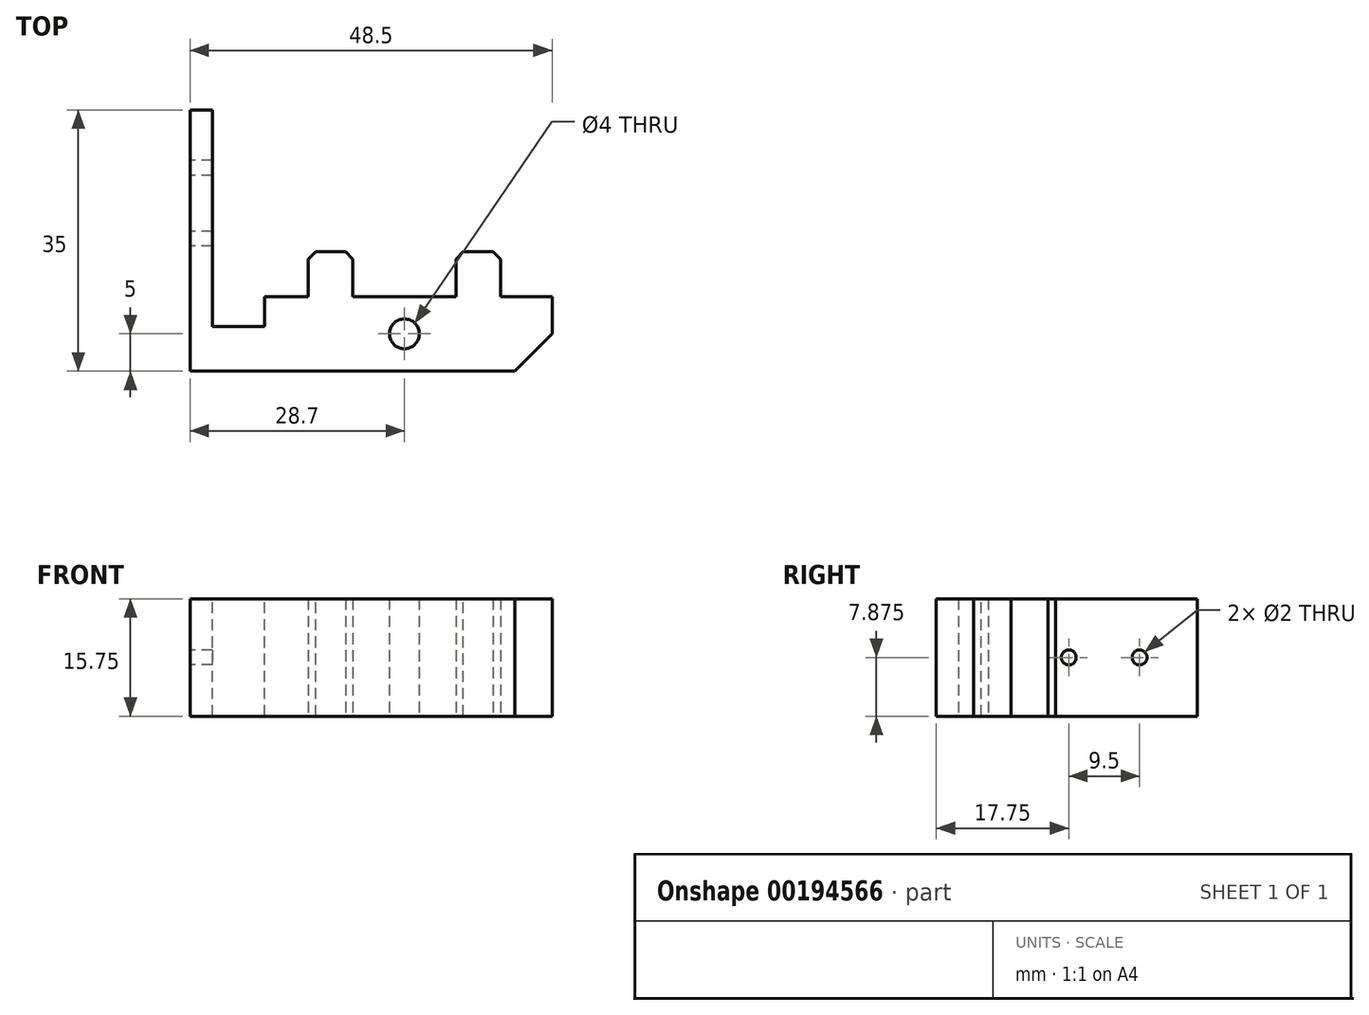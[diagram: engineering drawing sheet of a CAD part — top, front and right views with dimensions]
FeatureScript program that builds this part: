
annotation { "Feature Type Name" : "Feature", "Feature Type Description" : "" }
export const myFeature = defineFeature(function(context is Context, id is Id, definition is map)
    precondition{}
    {
        {
            var Q0;
            Q0=qCreatedBy(makeId("Top.planeOp"),FACE);
            var sketch = newSketch(context, id + "F0", { "sketchPlane" : qUnion([Q0])});
            skLineSegment(sketch, "E0", {"start": v(44.5, 0) * mm, "end": v(44.5, 10) * mm});
            skLineSegment(sketch, "E1", {"start": v(44.5, 10) * mm, "end": v(37.6, 10) * mm});
            skLineSegment(sketch, "E2", {"start": v(37.6, 10) * mm, "end": v(37.6, 16) * mm});
            skLineSegment(sketch, "E3", {"start": v(37.6, 16) * mm, "end": v(31.6, 16) * mm});
            skLineSegment(sketch, "E4", {"start": v(31.6, 16) * mm, "end": v(31.6, 10) * mm});
            skLineSegment(sketch, "E5", {"start": v(31.6, 10) * mm, "end": v(17.8, 10) * mm});
            skLineSegment(sketch, "E6", {"start": v(17.8, 10) * mm, "end": v(17.8, 16) * mm});
            skLineSegment(sketch, "E7", {"start": v(17.8, 16) * mm, "end": v(11.8, 16) * mm});
            skLineSegment(sketch, "E8", {"start": v(11.8, 16) * mm, "end": v(11.8, 10) * mm});
            skLineSegment(sketch, "E9", {"start": v(11.8, 10) * mm, "end": v(0, 10) * mm});
            skLineSegment(sketch, "E10", {"start": v(0, 0) * mm, "end": v(44.5, 0) * mm});
            skLineSegment(sketch, "E11", {"start": v(0, 10) * mm, "end": v(0, 0) * mm});
            skSolve(sketch);
        }
        {
            var Q0;
            Q0=qSketchRegion(id+"F0",true);
            extrude(context, id + "F1", {"entities" : qUnion([Q0]), "depth" : 15.75 * mm});
        }
        {
            var Q0;
            Q0=makeQuery(id+"F1.opExtrude","SWEPT_FACE",FACE,{"disambiguationData":[OSD([sQuery(id+"F0.wireOp",EDGE,"E10")])]});
            var sketch = newSketch(context, id + "F2", { "sketchPlane" : qUnion([Q0])});
            skLineSegment(sketch, "E12", {"start": v(0, 12.75) * mm, "end": v(15, 12.75) * mm});
            skLineSegment(sketch, "E13", {"start": v(15, 12.75) * mm, "end": v(15, 3) * mm});
            skLineSegment(sketch, "E14", {"start": v(15, 3) * mm, "end": v(0, 3) * mm});
            skLineSegment(sketch, "E15", {"start": v(0, 12.75) * mm, "end": v(0, 3) * mm});
            skSolve(sketch);
        }
        {
            var Q0;
            Q0=makeQuery(id+"F1.opExtrude","CAP_FACE",FACE,{"disambiguationData":[OSD([sQuery(id+"F0.wireOp",EDGE,"E0"),sQuery(id+"F0.wireOp",EDGE,"E1"),sQuery(id+"F0.wireOp",EDGE,"E2"),sQuery(id+"F0.wireOp",EDGE,"E3"),sQuery(id+"F0.wireOp",EDGE,"E4"),sQuery(id+"F0.wireOp",EDGE,"E5"),sQuery(id+"F0.wireOp",EDGE,"E6"),sQuery(id+"F0.wireOp",EDGE,"E7"),sQuery(id+"F0.wireOp",EDGE,"E8"),sQuery(id+"F0.wireOp",EDGE,"E9"),sQuery(id+"F0.wireOp",EDGE,"E10"),sQuery(id+"F0.wireOp",EDGE,"E11")])],"isStart":false});
            var sketch = newSketch(context, id + "F3", { "sketchPlane" : qUnion([Q0])});
            skPoint(sketch, "E16", {"position": v(24.7, 5) * mm});
            skPoint(sketch, "E16.positionSnap0", {"position": v(44.5, 5) * mm});
            skPoint(sketch, "E16.positionSnap1", {"position": v(24.7, 10) * mm});
            skSolve(sketch);
        }
        {
            var Q0;
            Q0=sQuery(id+"F3.wireOp",VERTEX,"E16");
            var Q1;
            Q1=makeQuery(id+"F1.opExtrude","SWEPT_BODY",BODY,{"disambiguationData":[OSD([sQuery(id+"F0.wireOp",EDGE,"E0"),sQuery(id+"F0.wireOp",EDGE,"E1"),sQuery(id+"F0.wireOp",EDGE,"E2"),sQuery(id+"F0.wireOp",EDGE,"E3"),sQuery(id+"F0.wireOp",EDGE,"E4"),sQuery(id+"F0.wireOp",EDGE,"E5"),sQuery(id+"F0.wireOp",EDGE,"E6"),sQuery(id+"F0.wireOp",EDGE,"E7"),sQuery(id+"F0.wireOp",EDGE,"E8"),sQuery(id+"F0.wireOp",EDGE,"E9"),sQuery(id+"F0.wireOp",EDGE,"E10"),sQuery(id+"F0.wireOp",EDGE,"E11")])]});
            hole(context, id + "F4", {"style" : HoleStyle.SIMPLE, "endStyle" : HoleEndStyle.THROUGH, "holeDiameter" : 4 * mm, "locations" : qUnion([Q0]), "scope" : qUnion([Q1]), "isTappedThrough" : true, "startStyle" : HoleStartStyle.PART});
        }
        {
            var Q0;
            Q0=makeQuery(id+"F1.opExtrude","SWEPT_FACE",FACE,{"disambiguationData":[OSD([sQuery(id+"F0.wireOp",EDGE,"E11")])]});
            extrude(context, id + "F5", {"entities" : qUnion([Q0]), "operationType" : NewBodyOperationType.ADD, "depth" : 3 * mm});
        }
        {
            var Q0;
            {var subQ0=sQuery(id+"F0.wireOp",EDGE,"E9");Q0=makeQuery(id+"F5.boolean.opBoolean","MERGE",FACE,{"derivedFrom":[makeQuery(id+"F1.opExtrude","SWEPT_FACE",FACE,{"disambiguationData":[OSD([subQ0])]}),makeQuery(id+"F5.opExtrude","SWEPT_FACE",FACE,{"disambiguationData":[OSD([subQ0,sQuery(id+"F0.wireOp",EDGE,"E11")])]})]});}
            var sketch = newSketch(context, id + "F6", { "sketchPlane" : qUnion([Q0])});
            skLineSegment(sketch, "E17", {"start": v(0, 0) * mm, "end": v(0, 15.75) * mm});
            skSolve(sketch);
        }
        {
            var Q0;
            {var subQ0=sQuery(id+"F6.wireOp",EDGE,"E17");Q0=makeQuery(id+"F6.imprint","IMPRINT",FACE,{"disambiguationData":[TD([[makeQuery(id+"F6.imprint","IMPRINT",EDGE,{"derivedFrom":subQ0}),-1.0]])]});}
            extrude(context, id + "F7", {"entities" : qUnion([Q0]), "operationType" : NewBodyOperationType.ADD, "depth" : 25 * mm});
        }
        {
            var Q0;
            Q0=makeQuery(id+"F7.opExtrude","SWEPT_FACE",FACE,{"disambiguationData":[OSD([sQuery(id+"F6.wireOp",EDGE,"E17")])]});
            var sketch = newSketch(context, id + "F8", { "sketchPlane" : qUnion([Q0])});
            skPoint(sketch, "E18", {"position": v(27.25, 7.88) * mm});
            skPoint(sketch, "E18.positionSnap0", {"position": v(35, 7.88) * mm});
            skPoint(sketch, "E19", {"position": v(17.75, 7.88) * mm});
            skLineSegment(sketch, "E20", {"start": v(27.25, 7.88) * mm, "end": v(35, 7.88) * mm, "construction": true});
            skLineSegment(sketch, "E21", {"start": v(17.75, 7.88) * mm, "end": v(10, 7.88) * mm, "construction": true});
            skSolve(sketch);
        }
        {
            var Q0;
            Q0=sQuery(id+"F8.wireOp",VERTEX,"E18");
            var Q1;
            Q1=sQuery(id+"F8.wireOp",VERTEX,"E19");
            var Q2;
            Q2=makeQuery(id+"F1.opExtrude","SWEPT_BODY",BODY,{"disambiguationData":[OSD([sQuery(id+"F0.wireOp",EDGE,"E0"),sQuery(id+"F0.wireOp",EDGE,"E1"),sQuery(id+"F0.wireOp",EDGE,"E2"),sQuery(id+"F0.wireOp",EDGE,"E3"),sQuery(id+"F0.wireOp",EDGE,"E4"),sQuery(id+"F0.wireOp",EDGE,"E5"),sQuery(id+"F0.wireOp",EDGE,"E6"),sQuery(id+"F0.wireOp",EDGE,"E7"),sQuery(id+"F0.wireOp",EDGE,"E8"),sQuery(id+"F0.wireOp",EDGE,"E9"),sQuery(id+"F0.wireOp",EDGE,"E10"),sQuery(id+"F0.wireOp",EDGE,"E11")])]});
            hole(context, id + "F9", {"style" : HoleStyle.SIMPLE, "endStyle" : HoleEndStyle.THROUGH, "holeDiameter" : 2 * mm, "locations" : qUnion([Q0, Q1]), "scope" : qUnion([Q2]), "isTappedThrough" : true, "startStyle" : HoleStartStyle.SKETCH});
        }
        {
            var Q0;
            {var subQ0=sQuery(id+"F0.wireOp",EDGE,"E11");var subQ1=sQuery(id+"F0.wireOp",EDGE,"E9");var subQ2=makeQuery(id+"F5.boolean.opBoolean","MERGE",EDGE,{"derivedFrom":[makeQuery(id+"F1.opExtrude","CAP_EDGE",EDGE,{"disambiguationData":[OSD([subQ1])],"isStart":false}),makeQuery(id+"F5.opExtrude","SWEPT_EDGE",EDGE,{"disambiguationData":[OSD([subQ1,subQ0]),TDD([makeQuery(id+"F1.opExtrude","CAP_VERTEX",VERTEX,{"disambiguationData":[OSD([subQ1,subQ0])],"isStart":false})])]})]});Q0=makeQuery(id+"F7.boolean.opBoolean","MERGE",FACE,{"derivedFrom":[makeQuery(id+"F5.boolean.opBoolean","MERGE",FACE,{"derivedFrom":[makeQuery(id+"F1.opExtrude","CAP_FACE",FACE,{"disambiguationData":[OSD([sQuery(id+"F0.wireOp",EDGE,"E0"),sQuery(id+"F0.wireOp",EDGE,"E1"),sQuery(id+"F0.wireOp",EDGE,"E2"),sQuery(id+"F0.wireOp",EDGE,"E3"),sQuery(id+"F0.wireOp",EDGE,"E4"),sQuery(id+"F0.wireOp",EDGE,"E5"),sQuery(id+"F0.wireOp",EDGE,"E6"),sQuery(id+"F0.wireOp",EDGE,"E7"),sQuery(id+"F0.wireOp",EDGE,"E8"),subQ1,sQuery(id+"F0.wireOp",EDGE,"E10"),subQ0])],"isStart":false}),makeQuery(id+"F5.opExtrude","SWEPT_FACE",FACE,{"disambiguationData":[OSD([subQ0]),TDD([makeQuery(id+"F1.opExtrude","CAP_EDGE",EDGE,{"disambiguationData":[OSD([subQ0])],"isStart":false})])]})]}),makeQuery(id+"F7.opExtrude","SWEPT_FACE",FACE,{"disambiguationData":[OSD([subQ1,subQ0]),TDD([makeQuery(id+"F6.imprint","IMPRINT",EDGE,{"disambiguationData":[TD([[makeQuery(id+"F6.imprint","INTERSECT",VERTEX,{"derivedFrom":[subQ2,sQuery(id+"F6.wireOp",EDGE,"E17")]}),-1.0]])],"derivedFrom":subQ2})])]})]});}
            var sketch = newSketch(context, id + "F10", { "sketchPlane" : qUnion([Q0])});
            skLineSegment(sketch, "E22", {"start": v(0, 10) * mm, "end": v(0, 6) * mm});
            skLineSegment(sketch, "E23", {"start": v(0, 6) * mm, "end": v(6, 6) * mm});
            skLineSegment(sketch, "E24", {"start": v(6, 6) * mm, "end": v(6, 10) * mm});
            skLineSegment(sketch, "E25", {"start": v(6, 10) * mm, "end": v(0, 10) * mm});
            skSolve(sketch);
        }
        {
            var Q0;
            Q0=qSketchRegion(id+"F10",true);
            extrude(context, id + "F11", {"entities" : qUnion([Q0]), "operationType" : NewBodyOperationType.REMOVE, "endBound" : BoundingType.THROUGH_ALL, "oppositeDirection" : true, "depth" : 25 * mm});
        }
        {
            var Q0;
            Q0=makeQuery(id+"F1.opExtrude","SWEPT_EDGE",EDGE,{"disambiguationData":[OSD([sQuery(id+"F0.wireOp",EDGE,"E7"),sQuery(id+"F0.wireOp",EDGE,"E8")])]});
            var Q1;
            Q1=makeQuery(id+"F1.opExtrude","SWEPT_EDGE",EDGE,{"disambiguationData":[OSD([sQuery(id+"F0.wireOp",EDGE,"E6"),sQuery(id+"F0.wireOp",EDGE,"E7")])]});
            var Q2;
            Q2=makeQuery(id+"F1.opExtrude","SWEPT_EDGE",EDGE,{"disambiguationData":[OSD([sQuery(id+"F0.wireOp",EDGE,"E3"),sQuery(id+"F0.wireOp",EDGE,"E4")])]});
            var Q3;
            Q3=makeQuery(id+"F1.opExtrude","SWEPT_EDGE",EDGE,{"disambiguationData":[OSD([sQuery(id+"F0.wireOp",EDGE,"E2"),sQuery(id+"F0.wireOp",EDGE,"E3")])]});
            chamfer(context, id + "F12", {"entities" : qUnion([Q0, Q1, Q2, Q3]), "width" : 1 * mm, "tangentPropagation" : true});
        }
        {
            var Q0;
            Q0=makeQuery(id+"F1.opExtrude","SWEPT_EDGE",EDGE,{"disambiguationData":[OSD([sQuery(id+"F0.wireOp",EDGE,"E0"),sQuery(id+"F0.wireOp",EDGE,"E10")])]});
            chamfer(context, id + "F13", {"entities" : qUnion([Q0]), "width" : 5 * mm, "tangentPropagation" : true});
        }
        {
            var Q0;
            {var subQ0=sQuery(id+"F0.wireOp",EDGE,"E11");var subQ1=sQuery(id+"F0.wireOp",EDGE,"E9");Q0=makeQuery(id+"F7.boolean.opBoolean","MERGE",FACE,{"derivedFrom":[makeQuery(id+"F5.opExtrude","CAP_FACE",FACE,{"disambiguationData":[OSD([subQ0])],"isStart":false}),makeQuery(id+"F7.opExtrude","SWEPT_FACE",FACE,{"disambiguationData":[OSD([subQ1,subQ0]),TDD([makeQuery(id+"F6.imprint","IMPRINT",EDGE,{"derivedFrom":makeQuery(id+"F5.opExtrude","CAP_EDGE",EDGE,{"disambiguationData":[OSD([subQ1,subQ0])],"isStart":false})})])]})]});}
            extrude(context, id + "F14", {"entities" : qUnion([Q0]), "operationType" : NewBodyOperationType.ADD, "depth" : 1 * mm});
        }
        {
            var Q0;
            Q0=makeQuery(id+"F11.boolean.opBoolean","MERGE",FACE,{"derivedFrom":[makeQuery(id+"F7.opExtrude","SWEPT_FACE",FACE,{"disambiguationData":[OSD([sQuery(id+"F6.wireOp",EDGE,"E17")])]}),makeQuery(id+"F11.opExtrude","SWEPT_FACE",FACE,{"disambiguationData":[OSD([sQuery(id+"F10.wireOp",EDGE,"E22")])]})]});
            extrude(context, id + "F15", {"entities" : qUnion([Q0]), "operationType" : NewBodyOperationType.REMOVE, "oppositeDirection" : true, "depth" : 1 * mm});
        }
    });
